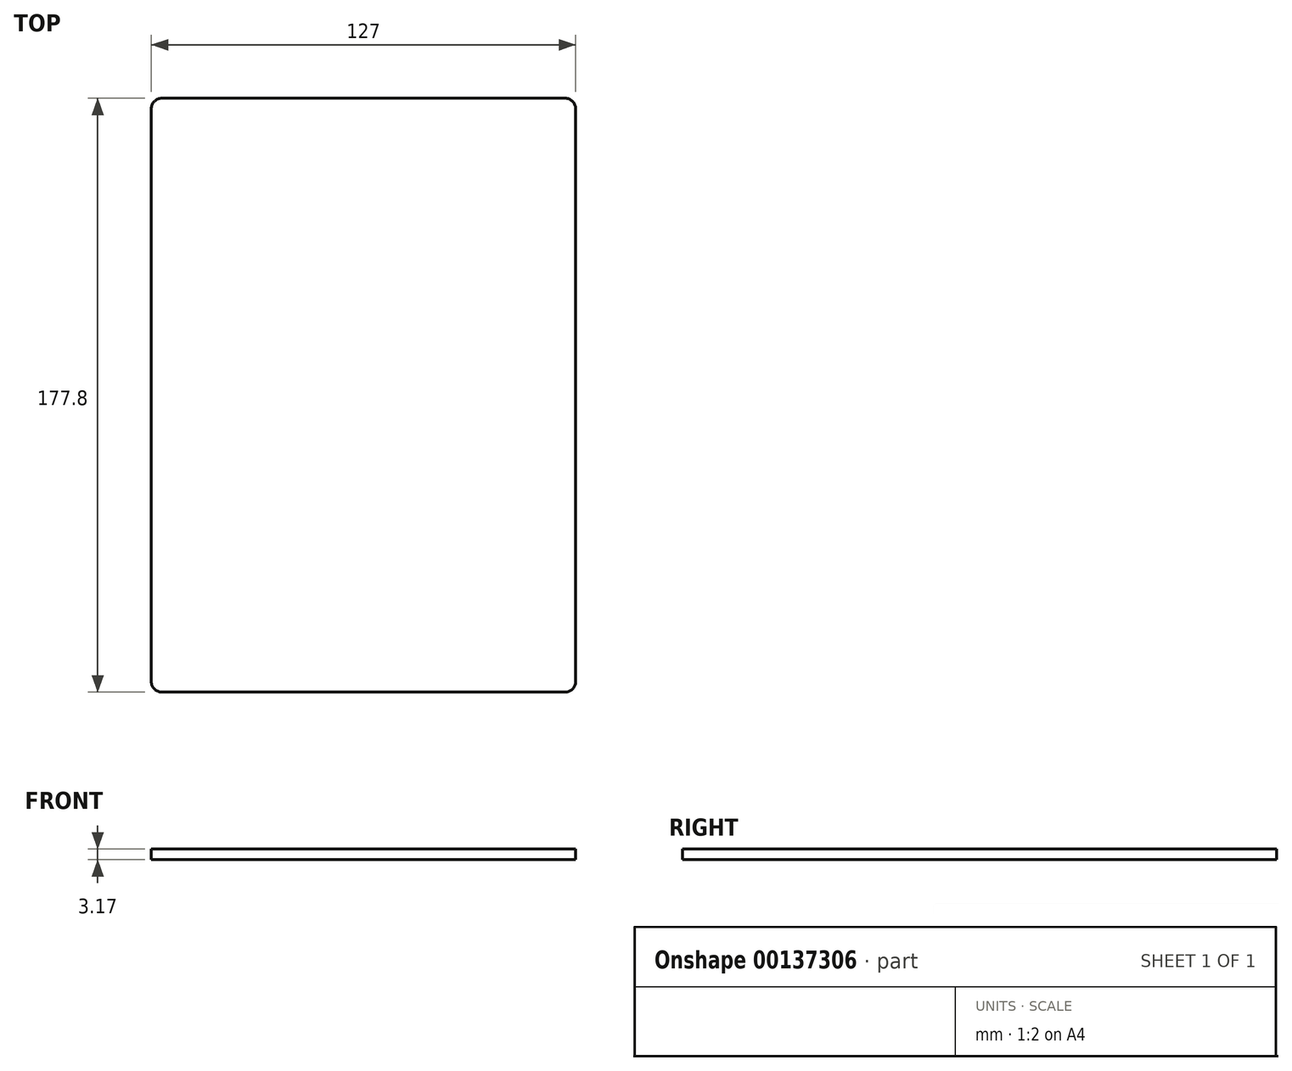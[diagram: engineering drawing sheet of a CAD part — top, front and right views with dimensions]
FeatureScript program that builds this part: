
annotation { "Feature Type Name" : "Feature", "Feature Type Description" : "" }
export const myFeature = defineFeature(function(context is Context, id is Id, definition is map)
    precondition{}
    {
        {
            var Q0;
            Q0=qCreatedBy(makeId("Top.planeOp"),FACE);
            var sketch = newSketch(context, id + "F0", { "sketchPlane" : qUnion([Q0])});
            skLineSegment(sketch, "E0.bottom", {"start": v(3.17, 0) * mm, "end": v(123.83, 0) * mm});
            skLineSegment(sketch, "E0.top", {"start": v(3.17, 177.8) * mm, "end": v(123.82, 177.8) * mm});
            skLineSegment(sketch, "E0.left", {"start": v(0, 3.17) * mm, "end": v(0, 174.62) * mm});
            skLineSegment(sketch, "E0.right", {"start": v(127, 3.17) * mm, "end": v(127, 174.62) * mm});
            skPoint(sketch, "E1.visualSharp", {"position": v(0, 177.8) * mm});
            skArc(sketch, "E1.filletArc", {"start": v(3.17, 177.8) * mm, "mid": v(0.93, 176.87) * mm, "end": v(0, 174.62) * mm});
            skPoint(sketch, "E2.visualSharp", {"position": v(127, 177.8) * mm});
            skArc(sketch, "E2.filletArc", {"start": v(127, 174.62) * mm, "mid": v(126.07, 176.87) * mm, "end": v(123.82, 177.8) * mm});
            skPoint(sketch, "E3.visualSharp", {"position": v(127, 0) * mm});
            skArc(sketch, "E3.filletArc", {"start": v(123.83, 0) * mm, "mid": v(126.07, 0.93) * mm, "end": v(127, 3.17) * mm});
            skPoint(sketch, "E4.visualSharp", {"position": v(0, 0) * mm});
            skArc(sketch, "E4.filletArc", {"start": v(0, 3.17) * mm, "mid": v(0.93, 0.93) * mm, "end": v(3.17, 0) * mm});
            skSolve(sketch);
        }
        {
            var Q0;
            Q0 = qSketchRegion(id + "F0", true);
            extrude(context, id + "F1", {"entities" : qUnion([Q0]), "depth" : 3.17 * mm});
        }
    });
